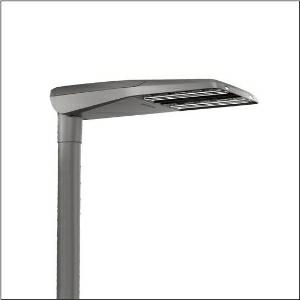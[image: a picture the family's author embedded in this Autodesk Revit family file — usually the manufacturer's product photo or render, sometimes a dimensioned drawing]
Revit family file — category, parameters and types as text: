
# Revit family: streetlight_sl_11_iq_midi___st0_5a_5xc3b51e08me_9498
name_source: partatom
category: Lighting Fixtures
units: mm (PartAtom-declared; Revit-internal decimal feet)

## family parameters
Cut with Voids When Loaded = No
Host = Face
Light Source = No
Part Type = Normal
Room Calculation Point = No
Round Connector Dimension = Use Diameter
Shared = No

## types (1)
- --- (1 x LED, 17940 lm, 124.7 W, 3000K)
    Apparent Load = 125 VA
    CIE Flux Codes = 43 74 97 100 100
    Color Rendering = 70
    Color Temperature = 3000K
    Default Elevation = 1800 mm
    Description = Streetlight SL 11 iQ midi, mast luminaire, primary light control with 3 zone facetted reflector, of plastic, silver coated, highly specular, primary optical cover: cover, of PMMA, transparent, light distribution: ST0.5a, light emission: direct distribution, primary light characteristic: asymmetric, installation type: post-top, side-entry, LED, High Power LED, rated luminous flux: 17.940lm, luminous efficacy: 144lm/W, light colour: 730, colour temperature: 3000K, control: optimised constant luminous flux control (CLO 2.0), Desk-Remote (wireless, voltage-free reading and setting of iQ features in the workshop via application-optimized NFC function/RFID function), Light-Fading, Smart-Wire, Night-Set, Lumen-Switch, Temp-Guard, Auto-Match, with cable H07RN-F 5x 1.5mm², mains connection: 220..240V, AC, 50/60Hz, connection cable pre-assembled, cable length: 12,5m, start of lifetime: 125W, end of lifetime: 132W, reduction: 61W, luminaire housing, of diecast aluminium, powder-coated, Siteco® metallic grey (DB 702S), length: 780mm, width: 376mm, height: 118mm, spigot size: 60/76mm (post-top) and 42/60/76mm (side-entry), mast flange for spigot size: 42mm: 5XC10008XM4, 60mm: 5XC10008XM2, 76/60mm: 5XC10108XM1, equipment: Power, protection rating (complete): IP66, insulation class (complete): insulation class II (safety insulation), certification: CE, ENEC, VDE, impact resistance: IK09, permissible operating ambient temperature for outdoor applications: -25..+50°C, standard-compliant lighting for roads and squares, packaging unit: 1 piece

Light Distribution: ST0.5a
    Height = 118 mm
    Lamp = 1 x LED
    Lamp Light Flux = 17940 lm
    Lamp Power = 124.7 W
    Lamp count = 1
    Length = 780 mm
    Luminous efficacy = 144 lm/W
    Manufacturer = Siteco
    ModVariant = No
    Model = 5XC3B51E08ME
    Number of Poles = 1
    OnlyDefault = Yes
    Power Factor = 1
    Product Name = Streetlight SL 11 iQ midi | ST0.5a
    Product group = mast luminaire | pylon top
    ProductGroupID = 6100
    Protection Class = Protection class II
    Protection Degree = IP 66
    RLX_Detail_Level = 1
    RlxData = <blob elided: 75149 chars, md5=344b9315>
    Socket = socket
    Standby Power = 0 W
    System Light Flux = 17941 lm
    System Power = 125 W
    Type Comments = factory setting: luminous flux: 100 % | dim-lin: 254 | 557 mA
    Type Image = l_1005960.jpg
    URL = http://relux.com
    VarID = @adj_086707
    Voltage = 0 V
    Weight = 0.00 kg
    Width = 376 mm

## geometry (parser evidence)
native form markers: Blend x4, Sweep x11
no freeform markers — native parametric forms only
